# Revit family: Drinking_Fountain_Bottle_Filler-Whitehall-BestCare-WHBF6
name_source: partatom
category: Plumbing Fixtures
revit_build: Autodesk Revit 2018 (Build: 20170223_1515(x64)
units: mm (PartAtom-declared; Revit-internal decimal feet)

## family parameters
Cut with Voids When Loaded = No
Host = Face
OmniClass Number = 23.65.70.14.11
OmniClass Title = Drinking Fountains/Coolers
Part Type = Normal
Room Calculation Point = No
Round Connector Dimension = Use Diameter
Shared = Yes

## types (1)
- WHBF6
    -BAT Battery Operated Sensors = No
    -MC Concealed Mounting Carrier = No
    -WF1 1500-Gallon Capacity, NSF 42+53, 1-Micron Lead Reduction Filter = No
    -WF3 3000-Gallon Capacity, NSF 42+53, 1-Micron Lead Reduction Filte = No
    A9100080 - A Remote Chiller, 8 Gallons Per Hour = No
    ADA Compliant = Yes
    Assembly Code = D2010800
    Bottle Filler Material = Stainless Steel-Whitehall-Type 304-Powder Coated White
    Bottom Enclosure Material = Stainless Steel-Whitehall-Type 304-Powder Coated White
    CW Connection = Yes
    CWFU = 1.5
    Cold Water Connection Diameter = 3/8"
    Cold Water Connection Height = 21 1/2"
    Cold Water Connection Width = 2 5/8"
    Default Elevation = 31 3/4"
    Description = BestCare® Ligature-Resistant Drink Fountain with Bottle Filler - ADA Compliant
    Drinking Fountain Material = Stainless Steel-Whitehall-Type 304-Powder Coated White
    Fill Rate = 1.0 GPM (3.8 LPM)
    HW Connection = No
    HWFU = 0
    Height = 49 3/4"
    IAPMO Compliance = Unit is certified to ANSI A117.1, Public Law111-380(NO-LEAD),CHSC116875and NSF/ANSI 61, Section
    Installation Type = Wall Mounted
    Length = 24 3/8"
    Manufacturer = Whitehall Manufacturing
    Model = WHBF6
    Power = 120 VAC
    Product Documentation Link = https://www.whitehallmfg.com
    Product Page URL = https://www.whitehallmfg.com
    Revised Date = 06/25/2021
    Strainer Material = Metal-Whitehall-Stainless Steel
    URL = http://www.whitehallmfg.com
    Vent Connection = No
    WFU = 2
    Waste Connection = Yes
    Waste Connection Height = 25 1/4"
    Water Connection Diameter = 1 1/2"
    Width = 21"

## geometry (parser evidence)
native form markers: Sweep x2
no freeform markers — native parametric forms only
